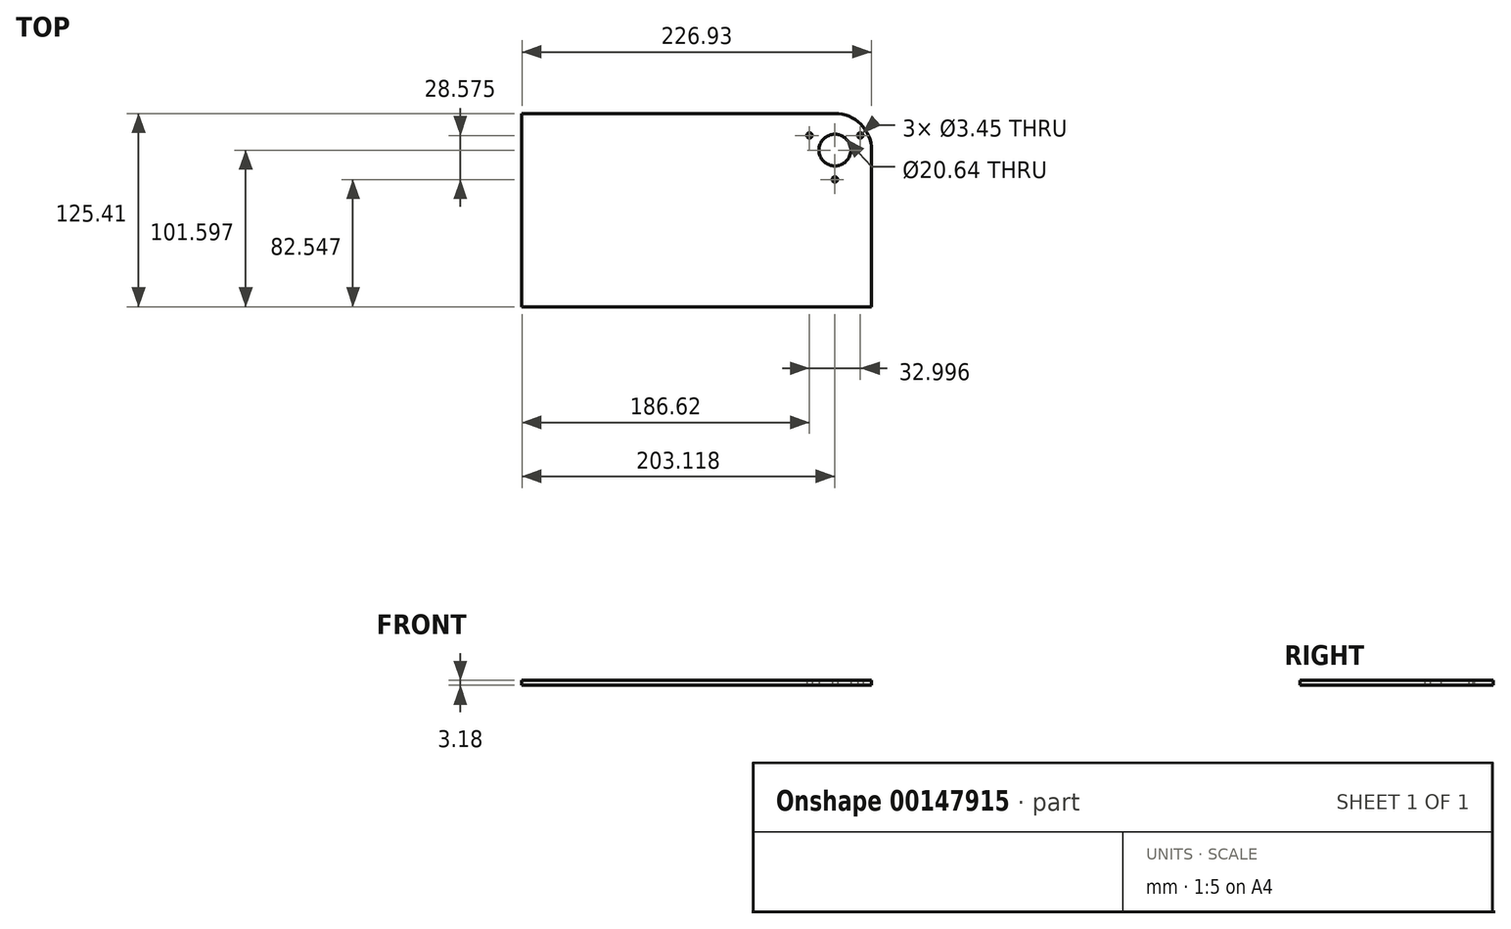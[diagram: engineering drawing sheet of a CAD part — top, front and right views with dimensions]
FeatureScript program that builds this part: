
annotation { "Feature Type Name" : "Feature", "Feature Type Description" : "" }
export const myFeature = defineFeature(function(context is Context, id is Id, definition is map)
    precondition{}
    {
        {
            var Q0;
            Q0=qCreatedBy(makeId("Top.planeOp"),FACE);
            var sketch = newSketch(context, id + "F0", { "sketchPlane" : qUnion([Q0])});
            skCircle(sketch, "E0", {"center": v(-23.81, -23.81) * mm, "radius": 10.32 * mm});
            skCircle(sketch, "E1.cCircle", {"center": v(-23.81, -23.81) * mm, "radius": 9.52 * mm, "construction": true});
            skLineSegment(sketch, "E1.0", {"start": v(-40.31, -14.29) * mm, "end": v(-7.31, -14.29) * mm, "construction": true});
            skLineSegment(sketch, "E1.1", {"start": v(-7.31, -14.29) * mm, "end": v(-23.81, -42.86) * mm, "construction": true});
            skLineSegment(sketch, "E1.2", {"start": v(-23.81, -42.86) * mm, "end": v(-40.31, -14.29) * mm, "construction": true});
            skPoint(sketch, "E1.0.midPoint", {"position": v(-23.81, -14.29) * mm});
            skCircle(sketch, "E2", {"center": v(-23.81, -23.81) * mm, "radius": 14.29 * mm, "construction": true});
            skCircle(sketch, "E3", {"center": v(-40.31, -14.29) * mm, "radius": 4.76 * mm, "construction": true});
            skCircle(sketch, "E4", {"center": v(-40.31, -14.29) * mm, "radius": 1.73 * mm});
            skCircle(sketch, "E5", {"center": v(-7.31, -14.29) * mm, "radius": 1.73 * mm});
            skCircle(sketch, "E6", {"center": v(-23.81, -42.86) * mm, "radius": 1.73 * mm});
            skLineSegment(sketch, "E7.bottom", {"start": v(-226.93, 0) * mm, "end": v(0, 0) * mm});
            skLineSegment(sketch, "E7.top", {"start": v(-226.93, -125.41) * mm, "end": v(0, -125.41) * mm});
            skLineSegment(sketch, "E7.left", {"start": v(-226.93, 0) * mm, "end": v(-226.93, -125.41) * mm});
            skLineSegment(sketch, "E7.right", {"start": v(0, 0) * mm, "end": v(0, -125.41) * mm});
            skCircle(sketch, "E8", {"center": v(-23.81, -23.81) * mm, "radius": 23.81 * mm, "construction": true});
            skSolve(sketch);
        }
        {
            var Q0;
            Q0=qSketchRegion(id+"F0",true);
            extrude(context, id + "F1", {"entities" : qUnion([Q0]), "depth" : 3.17 * mm});
        }
        {
            var Q0;
            Q0=makeQuery(id+"F1.opExtrude","SWEPT_EDGE",EDGE,{"disambiguationData":[OSD([sQuery(id+"F0.wireOp",EDGE,"E7.bottom"),sQuery(id+"F0.wireOp",EDGE,"E7.right")])]});
            fillet(context, id + "F2", {"entities" : qUnion([Q0]), "radius" : 23.8 * mm, "tangentPropagation" : true, "allowEdgeOverflow" : false});
        }
    });
